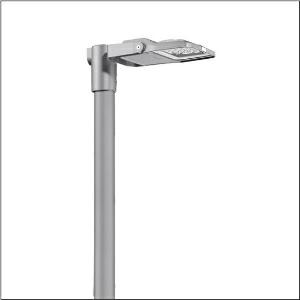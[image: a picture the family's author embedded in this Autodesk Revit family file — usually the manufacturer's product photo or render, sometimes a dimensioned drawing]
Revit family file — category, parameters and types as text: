
# Revit family: floodlight_fl_21_iq_micro___pl43_5xa7761a4a3a_9f97
name_source: partatom
category: Lighting Fixtures
units: mm (PartAtom-declared; Revit-internal decimal feet)

## family parameters
Cut with Voids When Loaded = No
Host = Face
Light Source = No
Part Type = Normal
Room Calculation Point = No
Round Connector Dimension = Use Diameter
Shared = No

## types (1)
- --- (1 x LED, 3170 lm, 23.1 W, 4000K)
    Apparent Load = 23 VA
    CIE Flux Codes = 29 80 99 100 100
    Color Rendering = 70
    Color Temperature = 4000K
    Default Elevation = 1800 mm
    Description = Floodlight FL 21 iQ micro, floodlight, primary light control with lens, of PMMA, primary optical cover: protective disc, of toughened safety glass, transparent, light distribution: PL43, light emission: direct distribution, installation type: surface-mounted, LED, High Power LED, rated luminous flux: 3.170lm, luminous efficacy: 137lm/W, light colour: 740, colour temperature: 4000K, control: optimised constant luminous flux control (CLO 2.0), Desk-Remote (wireless, voltage-free reading and setting of iQ features in the workshop via application-optimized NFC function/RFID function), Light-Fading, Smart-Wire, Night-Set, Lumen-Switch, Temp-Guard, Auto-Match, with terminal, 6-pole, mains connection: 220..240V, AC, 50/60Hz, start of lifetime: 23W, end of service life: 24W, reduction: 11W, luminaire housing, of diecast aluminium, powder-coated, Siteco® metallic grey (DB 702S), corrosivity category C5 mid according to DIN EN ISO 12944, sealing non-destructively replaceable, please order mast flange separately, mast bracket, of steel, galvanised, powder-coated, Siteco® metallic grey (DB 702S), protection rating (complete): IP66, insulation class (complete): insulation class II (safety insulation), certification: CE, ENEC, VDE, protection symbol: D, impact resistance: IK07, permissible operating ambient temperature: -40..+40°C, permissible operating ambient temperature for outdoor applications: -40..+50°C, standard: DIN EN 12944, LABS conformity tested according to VDMA 24364:2018-05, packaging unit: 1 piece

Light Distribution: PL43
    Height = 65 mm
    Lamp = 1 x LED
    Lamp Light Flux = 3170 lm
    Lamp Power = 23.1 W
    Lamp count = 1
    Length = 312 mm
    Luminous efficacy = 137 lm/W
    Manufacturer = Siteco
    ModVariant = No
    Model = 5XA7761A4A3A
    Number of Poles = 1
    OnlyDefault = Yes
    Power Factor = 1
    Product Name = Floodlight FL 21 iQ micro | PL43
    Product group = floodlight | pylon annexe
    ProductGroupID = 6200
    Protection Class = Protection class II
    Protection Degree = IP 66
    RLX_Detail_Level = 1
    RLX_Emergency_Light_Flux = 0 lm
    RLX_Emergency_Type = 0
    RLX_Emergency_Type_DB = No
    RlxData = <blob elided: 101525 chars, md5=ad27ce2b>
    Socket = socket
    Standby Power = 0 W
    System Light Flux = 3170 lm
    System Power = 23 W
    Type Comments = factory setting: luminous flux: 100 % | dim-lin: 254 | 455 mA
    Type Image = l_1007121.jpg
    URL = http://relux.com
    VarID = @adj_110093
    Voltage = 0 V
    Weight = 0.00 kg
    Width = 230 mm

## geometry (parser evidence)
native form markers: Blend x4, Sweep x12
no freeform markers — native parametric forms only
